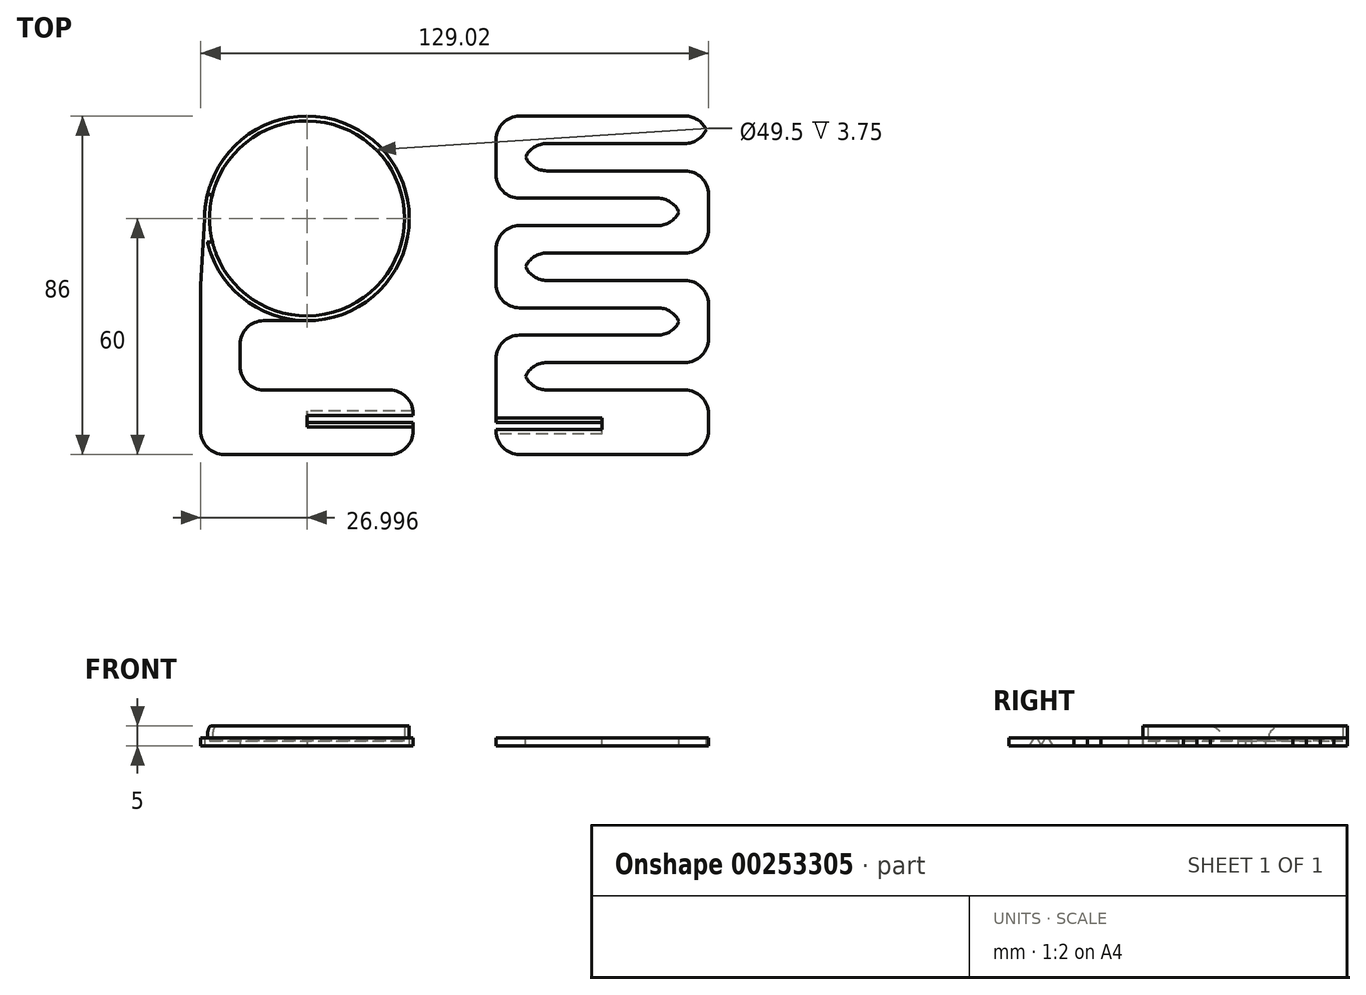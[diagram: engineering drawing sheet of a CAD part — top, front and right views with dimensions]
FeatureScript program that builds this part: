
annotation { "Feature Type Name" : "Feature", "Feature Type Description" : "" }
export const myFeature = defineFeature(function(context is Context, id is Id, definition is map)
    precondition{}
    {
        {
            var Q0;
            Q0=qCreatedBy(makeId("Top.planeOp"),FACE);
            cPlane(context, id + "F0", {"entities" : qUnion([Q0]), "cplaneType" : CPlaneType.OFFSET, "offset" : 2 * mm, "width" : 150 * mm, "height" : 150 * mm});
        }
        {
            var Q0;
            Q0=qCreatedBy(makeId("Top.planeOp"),FACE);
            var sketch = newSketch(context, id + "F1", { "sketchPlane" : qUnion([Q0])});
            skLineSegment(sketch, "E0.bottom", {"start": v(-64.51, -37.29) * mm, "end": v(-10.51, -37.29) * mm});
            skLineSegment(sketch, "E0.top", {"start": v(-64.51, 48.71) * mm, "end": v(-10.51, 48.71) * mm, "construction": true});
            skLineSegment(sketch, "E0.left", {"start": v(-64.51, -37.29) * mm, "end": v(-64.51, 48.71) * mm, "construction": true});
            skLineSegment(sketch, "E1", {"start": v(0, 56.35) * mm, "end": v(0, -54.54) * mm, "construction": true});
            skLineSegment(sketch, "E2.MirrorCS", {"start": v(64.51, 48.71) * mm, "end": v(10.51, 48.71) * mm});
            skLineSegment(sketch, "E3.MirrorCS", {"start": v(64.51, -37.29) * mm, "end": v(10.51, -37.29) * mm});
            skLineSegment(sketch, "E4.bottom", {"start": v(64.51, 41.75) * mm, "end": v(17.47, 41.75) * mm});
            skLineSegment(sketch, "E4.top", {"start": v(64.51, 34.8) * mm, "end": v(17.47, 34.8) * mm});
            skLineSegment(sketch, "E4.right", {"start": v(17.47, 41.75) * mm, "end": v(17.47, 34.8) * mm});
            skLineSegment(sketch, "E5.bottom", {"start": v(10.51, 27.83) * mm, "end": v(57.56, 27.83) * mm});
            skLineSegment(sketch, "E5.top", {"start": v(10.51, 20.88) * mm, "end": v(57.56, 20.88) * mm});
            skLineSegment(sketch, "E5.right", {"start": v(57.56, 27.83) * mm, "end": v(57.56, 20.88) * mm});
            skLineSegment(sketch, "E6.bottom", {"start": v(64.51, 13.92) * mm, "end": v(17.47, 13.92) * mm});
            skLineSegment(sketch, "E6.top", {"start": v(64.51, 6.96) * mm, "end": v(17.47, 6.96) * mm});
            skLineSegment(sketch, "E6.right", {"start": v(17.47, 13.92) * mm, "end": v(17.47, 6.96) * mm});
            skLineSegment(sketch, "E7.bottom", {"start": v(10.51, 0) * mm, "end": v(57.56, 0) * mm});
            skLineSegment(sketch, "E7.top", {"start": v(10.51, -6.96) * mm, "end": v(57.56, -6.96) * mm});
            skLineSegment(sketch, "E7.right", {"start": v(57.56, 0) * mm, "end": v(57.56, -6.96) * mm});
            skLineSegment(sketch, "E8.bottom", {"start": v(64.51, -13.92) * mm, "end": v(17.47, -13.92) * mm});
            skLineSegment(sketch, "E8.top", {"start": v(64.51, -20.88) * mm, "end": v(17.47, -20.88) * mm});
            skLineSegment(sketch, "E8.right", {"start": v(17.47, -13.92) * mm, "end": v(17.47, -20.88) * mm});
            skLineSegment(sketch, "E9", {"start": v(64.51, 48.71) * mm, "end": v(64.51, 41.75) * mm});
            skLineSegment(sketch, "E10", {"start": v(64.51, 34.8) * mm, "end": v(64.51, 13.92) * mm});
            skLineSegment(sketch, "E11", {"start": v(64.51, 6.96) * mm, "end": v(64.51, -13.92) * mm});
            skLineSegment(sketch, "E12", {"start": v(64.51, -20.88) * mm, "end": v(64.51, -37.29) * mm});
            skLineSegment(sketch, "E13", {"start": v(10.51, 48.71) * mm, "end": v(10.51, 27.83) * mm});
            skLineSegment(sketch, "E14", {"start": v(10.51, 20.88) * mm, "end": v(10.51, 0) * mm});
            skLineSegment(sketch, "E15", {"start": v(57.56, 27.83) * mm, "end": v(57.56, 34.8) * mm, "construction": true});
            skLineSegment(sketch, "E16", {"start": v(17.47, 13.92) * mm, "end": v(17.47, 20.88) * mm, "construction": true});
            skLineSegment(sketch, "E17", {"start": v(57.56, 0) * mm, "end": v(57.56, 6.96) * mm, "construction": true});
            skLineSegment(sketch, "E18", {"start": v(17.47, -13.92) * mm, "end": v(17.47, -6.96) * mm, "construction": true});
            skLineSegment(sketch, "E19", {"start": v(17.47, 34.8) * mm, "end": v(10.51, 34.8) * mm, "construction": true});
            skLineSegment(sketch, "E20", {"start": v(57.56, 20.88) * mm, "end": v(64.51, 20.88) * mm, "construction": true});
            skPoint(sketch, "E20.endSnap0", {"position": v(64.51, 24.36) * mm});
            skPoint(sketch, "E21.2.internal.snap0", {"position": v(-64.51, 5.71) * mm});
            skLineSegment(sketch, "E22", {"start": v(-64.51, 5.71) * mm, "end": v(-64.51, -37.29) * mm});
            skLineSegment(sketch, "E23.top", {"start": v(-10.51, -20.88) * mm, "end": v(-54.51, -20.88) * mm});
            skLineSegment(sketch, "E23.right", {"start": v(-54.51, -3.29) * mm, "end": v(-54.51, -20.88) * mm});
            skLineSegment(sketch, "E24", {"start": v(-54.51, -3.29) * mm, "end": v(-64.51, -3.29) * mm, "construction": true});
            skLineSegment(sketch, "E25", {"start": v(-37.51, 48.71) * mm, "end": v(-37.51, -3.29) * mm, "construction": true});
            skPoint(sketch, "E26.second.point", {"position": v(-37.51, -3.29) * mm});
            skPoint(sketch, "E26.third.point", {"position": v(-63.51, 22.71) * mm});
            skPoint(sketch, "E27.MirrorP", {"position": v(-11.51, 22.71) * mm});
            skLineSegment(sketch, "E28", {"start": v(-64.51, 5.71) * mm, "end": v(-63.51, 22.71) * mm});
            skLineSegment(sketch, "E29", {"start": v(17.47, 41.75) * mm, "end": v(17.47, 48.71) * mm, "construction": true});
            skLineSegment(sketch, "E30", {"start": v(-54.51, -3.29) * mm, "end": v(-37.51, -3.29) * mm});
            skArc(sketch, "E31", {"start": v(-63.51, 22.71) * mm, "mid": v(-55.9, 4.33) * mm, "end": v(-37.51, -3.29) * mm});
            skArc(sketch, "E32", {"start": v(-37.51, -3.29) * mm, "mid": v(-19.13, 41.1) * mm, "end": v(-63.51, 22.71) * mm, "construction": true});
            skLineSegment(sketch, "E33", {"start": v(-10.51, -20.88) * mm, "end": v(-10.51, -37.29) * mm});
            skLineSegment(sketch, "E34", {"start": v(10.51, -6.96) * mm, "end": v(10.51, -37.29) * mm});
            skLineSegment(sketch, "E35", {"start": v(-10.51, -29.08) * mm, "end": v(-64.51, -29.08) * mm, "construction": true});
            skLineSegment(sketch, "E36", {"start": v(64.51, -29.08) * mm, "end": v(10.51, -29.08) * mm, "construction": true});
            skSolve(sketch);
        }
        {
            var Q0;
            Q0=qCreatedBy(makeId("Top.planeOp"),FACE);
            var sketch = newSketch(context, id + "F2", { "sketchPlane" : qUnion([Q0])});
            skCircle(sketch, "E37", {"center": v(-37.51, 22.71) * mm, "radius": 26 * mm});
            skPoint(sketch, "E37.first.point", {"position": v(-37.51, 48.71) * mm});
            skPoint(sketch, "E37.second.point", {"position": v(-37.51, -3.29) * mm});
            skPoint(sketch, "E37.third.point", {"position": v(-63.51, 22.71) * mm});
            skSolve(sketch);
        }
        {
            var Q0;
            Q0=qCreatedBy(id+"F0.planeOp",FACE);
            var sketch = newSketch(context, id + "F3", { "sketchPlane" : qUnion([Q0])});
            skLineSegment(sketch, "E38.bottom", {"start": v(-67.51, 28.71) * mm, "end": v(-59.51, 28.71) * mm});
            skLineSegment(sketch, "E38.top", {"start": v(-67.51, 16.71) * mm, "end": v(-59.51, 16.71) * mm});
            skLineSegment(sketch, "E38.left", {"start": v(-67.51, 28.71) * mm, "end": v(-67.51, 16.71) * mm});
            skLineSegment(sketch, "E38.right", {"start": v(-59.51, 28.71) * mm, "end": v(-59.51, 16.71) * mm});
            skPoint(sketch, "E38.middle", {"position": v(-63.51, 22.71) * mm});
            skSolve(sketch);
        }
        {
            var Q0;
            Q0=qCreatedBy(makeId("Top.planeOp"),FACE);
            var sketch = newSketch(context, id + "F4", { "sketchPlane" : qUnion([Q0])});
            skLineSegment(sketch, "E39.bottom", {"start": v(-10.51, -33.93) * mm, "end": v(-37.51, -33.93) * mm});
            skLineSegment(sketch, "E39.top", {"start": v(-10.51, -24.24) * mm, "end": v(-37.51, -24.24) * mm});
            skLineSegment(sketch, "E39.left", {"start": v(-10.51, -33.93) * mm, "end": v(-10.51, -24.24) * mm});
            skLineSegment(sketch, "E39.right", {"start": v(-37.51, -33.93) * mm, "end": v(-37.51, -24.24) * mm});
            skPoint(sketch, "E39.middle", {"position": v(-24.01, -29.08) * mm});
            skSolve(sketch);
        }
        {
            var Q0;
            Q0=qCreatedBy(makeId("Top.planeOp"),FACE);
            var sketch = newSketch(context, id + "F5", { "sketchPlane" : qUnion([Q0])});
            skLineSegment(sketch, "E40.bottom", {"start": v(37.51, -24.24) * mm, "end": v(10.51, -24.24) * mm});
            skLineSegment(sketch, "E40.top", {"start": v(37.51, -33.93) * mm, "end": v(10.51, -33.93) * mm});
            skLineSegment(sketch, "E40.left", {"start": v(37.51, -24.24) * mm, "end": v(37.51, -33.93) * mm});
            skLineSegment(sketch, "E40.right", {"start": v(10.51, -24.24) * mm, "end": v(10.51, -33.93) * mm});
            skPoint(sketch, "E40.middle", {"position": v(24.01, -29.08) * mm});
            skSolve(sketch);
        }
        {
            var Q0;
            Q0 = qSketchRegion(id + "F1", true);
            extrude(context, id + "F6", {"entities" : qUnion([Q0]), "depth" : 2 * mm});
        }
        {
            var Q0;
            Q0=makeQuery(id+"F6.opExtrude","SWEPT_EDGE",EDGE,{"disambiguationData":[OSD([sQuery(id+"F1.wireOp",EDGE,"E4.bottom"),sQuery(id+"F1.wireOp",EDGE,"E4.right")])]});
            var Q1;
            Q1=makeQuery(id+"F6.opExtrude","SWEPT_EDGE",EDGE,{"disambiguationData":[OSD([sQuery(id+"F1.wireOp",EDGE,"E6.bottom"),sQuery(id+"F1.wireOp",EDGE,"E6.right")])]});
            var Q2;
            Q2=makeQuery(id+"F6.opExtrude","SWEPT_EDGE",EDGE,{"disambiguationData":[OSD([sQuery(id+"F1.wireOp",EDGE,"E8.bottom"),sQuery(id+"F1.wireOp",EDGE,"E8.right")])]});
            var Q3;
            Q3=makeQuery(id+"F6.opExtrude","SWEPT_EDGE",EDGE,{"disambiguationData":[OSD([sQuery(id+"F1.wireOp",EDGE,"E8.top"),sQuery(id+"F1.wireOp",EDGE,"E12")])]});
            var Q4;
            Q4=makeQuery(id+"F6.opExtrude","SWEPT_EDGE",EDGE,{"disambiguationData":[OSD([sQuery(id+"F1.wireOp",EDGE,"E8.bottom"),sQuery(id+"F1.wireOp",EDGE,"E11")])]});
            var Q5;
            Q5=makeQuery(id+"F6.opExtrude","SWEPT_EDGE",EDGE,{"disambiguationData":[OSD([sQuery(id+"F1.wireOp",EDGE,"E6.top"),sQuery(id+"F1.wireOp",EDGE,"E11")])]});
            var Q6;
            Q6=makeQuery(id+"F6.opExtrude","SWEPT_EDGE",EDGE,{"disambiguationData":[OSD([sQuery(id+"F1.wireOp",EDGE,"E6.bottom"),sQuery(id+"F1.wireOp",EDGE,"E10")])]});
            var Q7;
            Q7=makeQuery(id+"F6.opExtrude","SWEPT_EDGE",EDGE,{"disambiguationData":[OSD([sQuery(id+"F1.wireOp",EDGE,"E4.top"),sQuery(id+"F1.wireOp",EDGE,"E10")])]});
            var Q8;
            Q8=makeQuery(id+"F6.opExtrude","SWEPT_EDGE",EDGE,{"disambiguationData":[OSD([sQuery(id+"F1.wireOp",EDGE,"E2.MirrorCS"),sQuery(id+"F1.wireOp",EDGE,"E9")])]});
            var Q9;
            Q9=makeQuery(id+"F6.opExtrude","SWEPT_EDGE",EDGE,{"disambiguationData":[OSD([sQuery(id+"F1.wireOp",EDGE,"E3.MirrorCS"),sQuery(id+"F1.wireOp",EDGE,"E12")])]});
            var Q10;
            Q10=makeQuery(id+"F6.opExtrude","SWEPT_EDGE",EDGE,{"disambiguationData":[OSD([sQuery(id+"F1.wireOp",EDGE,"E3.MirrorCS"),sQuery(id+"F1.wireOp",EDGE,"b5c075ea-845a-4698-b512-59f1e6f9d4d20.MirrorCS")])]});
            var Q11;
            Q11=makeQuery(id+"F6.opExtrude","SWEPT_EDGE",EDGE,{"disambiguationData":[OSD([sQuery(id+"F1.wireOp",EDGE,"E0.bottom"),sQuery(id+"F1.wireOp",EDGE,"YFyWnAeK-pBBA-IvNz-k6wc-S340Zklw97iA")])]});
            var Q12;
            Q12=makeQuery(id+"F6.opExtrude","SWEPT_EDGE",EDGE,{"disambiguationData":[OSD([sQuery(id+"F1.wireOp",EDGE,"E0.bottom"),sQuery(id+"F1.wireOp",EDGE,"E0.left")])]});
            var Q13;
            Q13=makeQuery(id+"F6.opExtrude","SWEPT_EDGE",EDGE,{"disambiguationData":[OSD([sQuery(id+"F1.wireOp",EDGE,"E0.top"),sQuery(id+"F1.wireOp",EDGE,"n8BnLhJH-u2Um-0aWn-nEOY-44NhoaiNVUQD")])]});
            var Q14;
            Q14=makeQuery(id+"F6.opExtrude","SWEPT_EDGE",EDGE,{"disambiguationData":[OSD([sQuery(id+"F1.wireOp",EDGE,"E4.top"),sQuery(id+"F1.wireOp",EDGE,"E4.right")])]});
            var Q15;
            Q15=makeQuery(id+"F6.opExtrude","SWEPT_EDGE",EDGE,{"disambiguationData":[OSD([sQuery(id+"F1.wireOp",EDGE,"E6.top"),sQuery(id+"F1.wireOp",EDGE,"E6.right")])]});
            var Q16;
            Q16=makeQuery(id+"F6.opExtrude","SWEPT_EDGE",EDGE,{"disambiguationData":[OSD([sQuery(id+"F1.wireOp",EDGE,"E5.top"),sQuery(id+"F1.wireOp",EDGE,"E14")])]});
            var Q17;
            Q17=makeQuery(id+"F6.opExtrude","SWEPT_EDGE",EDGE,{"disambiguationData":[OSD([sQuery(id+"F1.wireOp",EDGE,"E7.top"),sQuery(id+"F1.wireOp",EDGE,"ZmS6kUhB-3YoN-C8Cs-CpPg-u5vmyANZ6dh0")])]});
            var Q18;
            Q18=makeQuery(id+"F6.opExtrude","SWEPT_EDGE",EDGE,{"disambiguationData":[OSD([sQuery(id+"F1.wireOp",EDGE,"E2.MirrorCS"),sQuery(id+"F1.wireOp",EDGE,"E13")])]});
            var Q19;
            Q19=makeQuery(id+"F6.opExtrude","SWEPT_EDGE",EDGE,{"disambiguationData":[OSD([sQuery(id+"F1.wireOp",EDGE,"E8.top"),sQuery(id+"F1.wireOp",EDGE,"E8.right")])]});
            var Q20;
            Q20=makeQuery(id+"F6.opExtrude","SWEPT_EDGE",EDGE,{"disambiguationData":[OSD([sQuery(id+"F1.wireOp",EDGE,"E7.bottom"),sQuery(id+"F1.wireOp",EDGE,"E7.right")])]});
            var Q21;
            Q21=makeQuery(id+"F6.opExtrude","SWEPT_EDGE",EDGE,{"disambiguationData":[OSD([sQuery(id+"F1.wireOp",EDGE,"E7.bottom"),sQuery(id+"F1.wireOp",EDGE,"E14")])]});
            var Q22;
            Q22=makeQuery(id+"F6.opExtrude","SWEPT_EDGE",EDGE,{"disambiguationData":[OSD([sQuery(id+"F1.wireOp",EDGE,"02cee5f8-0e07-4a12-8da6-797b128053240.MirrorCS"),sQuery(id+"F1.wireOp",EDGE,"ZmS6kUhB-3YoN-C8Cs-CpPg-u5vmyANZ6dh0")])]});
            var Q23;
            Q23=makeQuery(id+"F6.opExtrude","SWEPT_EDGE",EDGE,{"disambiguationData":[OSD([sQuery(id+"F1.wireOp",EDGE,"E5.bottom"),sQuery(id+"F1.wireOp",EDGE,"E13")])]});
            var Q24;
            Q24=makeQuery(id+"F6.opExtrude","SWEPT_EDGE",EDGE,{"disambiguationData":[OSD([sQuery(id+"F1.wireOp",EDGE,"E5.bottom"),sQuery(id+"F1.wireOp",EDGE,"E5.right")])]});
            var Q25;
            Q25=makeQuery(id+"F6.opExtrude","SWEPT_EDGE",EDGE,{"disambiguationData":[OSD([sQuery(id+"F1.wireOp",EDGE,"E0.top"),sQuery(id+"F1.wireOp",EDGE,"E0.left")])]});
            var Q26;
            Q26=makeQuery(id+"F6.opExtrude","SWEPT_EDGE",EDGE,{"disambiguationData":[OSD([sQuery(id+"F1.wireOp",EDGE,"E5.top"),sQuery(id+"F1.wireOp",EDGE,"E5.right")])]});
            var Q27;
            Q27=makeQuery(id+"F6.opExtrude","SWEPT_EDGE",EDGE,{"disambiguationData":[OSD([sQuery(id+"F1.wireOp",EDGE,"E7.top"),sQuery(id+"F1.wireOp",EDGE,"E7.right")])]});
            var Q28;
            Q28=makeQuery(id+"F6.opExtrude","SWEPT_EDGE",EDGE,{"disambiguationData":[OSD([sQuery(id+"F1.wireOp",EDGE,"E23.top"),sQuery(id+"F1.wireOp",EDGE,"E23.right")])]});
            var Q29;
            Q29=makeQuery(id+"F6.opExtrude","SWEPT_EDGE",EDGE,{"disambiguationData":[OSD([sQuery(id+"F1.wireOp",EDGE,"E23.top"),sQuery(id+"F1.wireOp",EDGE,"a9DOpzYk-i0cr-7vyi-HXUP-g6eablmnLJva")])]});
            var Q30;
            Q30=makeQuery(id+"F6.opExtrude","SWEPT_EDGE",EDGE,{"disambiguationData":[OSD([sQuery(id+"F1.wireOp",EDGE,"E23.bottom"),sQuery(id+"F1.wireOp",EDGE,"lBwJjgHI-4274-be9I-VBba-0aZR1f0Lvly4")])]});
            var Q31;
            Q31=makeQuery(id+"F6.opExtrude","SWEPT_EDGE",EDGE,{"disambiguationData":[OSD([sQuery(id+"F1.wireOp",EDGE,"E23.bottom"),sQuery(id+"F1.wireOp",EDGE,"E23.right")])]});
            var Q32;
            Q32=makeQuery(id+"F6.opExtrude","SWEPT_EDGE",EDGE,{"disambiguationData":[OSD([sQuery(id+"F1.wireOp",EDGE,"E4.bottom"),sQuery(id+"F1.wireOp",EDGE,"E9")])]});
            fillet(context, id + "F7", {"entities" : qUnion([Q0, Q1, Q2, Q3, Q4, Q5, Q6, Q7, Q8, Q9, Q10, Q11, Q12, Q13, Q14, Q15, Q16, Q17, Q18, Q19, Q20, Q21, Q22, Q23, Q24, Q25, Q26, Q27, Q28, Q29, Q30, Q31, Q32]), "radius" : 6 * mm, "tangentPropagation" : true, "allowEdgeOverflow" : false});
        }
        {
            var Q0;
            Q0 = qSketchRegion(id + "F2", true);
            extrude(context, id + "F8", {"entities" : qUnion([Q0]), "operationType" : NewBodyOperationType.ADD, "depth" : 5 * mm});
        }
        {
            var Q0;
            Q0=makeQuery(id+"F8.opExtrude","CAP_FACE",FACE,{"disambiguationData":[OSD([sQuery(id+"F2.wireOp",EDGE,"E37")])],"isStart":false});
            shell(context, id + "F9", {"entities" : qUnion([Q0]), "thickness" : 1.25 * mm});
        }
        {
            var Q0;
            Q0 = qSketchRegion(id + "F3", true);
            extrude(context, id + "F10", {"entities" : qUnion([Q0]), "operationType" : NewBodyOperationType.REMOVE, "depth" : 5 * mm});
        }
        {
            var Q0;
            Q0=makeQuery(id+"F10.boolean.opBoolean","INTERSECT",EDGE,{"derivedFrom":[makeQuery(id+"F8.opExtrude","CAP_FACE",FACE,{"disambiguationData":[OSD([sQuery(id+"F2.wireOp",EDGE,"E37")])],"isStart":false}),makeQuery(id+"F10.opExtrude","SWEPT_FACE",FACE,{"disambiguationData":[OSD([sQuery(id+"F3.wireOp",EDGE,"E38.bottom")])]})]});
            var Q1;
            Q1=makeQuery(id+"F10.boolean.opBoolean","INTERSECT",EDGE,{"derivedFrom":[makeQuery(id+"F8.opExtrude","CAP_FACE",FACE,{"disambiguationData":[OSD([sQuery(id+"F2.wireOp",EDGE,"E37")])],"isStart":false}),makeQuery(id+"F10.opExtrude","SWEPT_FACE",FACE,{"disambiguationData":[OSD([sQuery(id+"F3.wireOp",EDGE,"E38.top")])]})]});
            fillet(context, id + "F11", {"entities" : qUnion([Q0, Q1]), "radius" : 3 * mm, "tangentPropagation" : true, "allowEdgeOverflow" : false});
        }
        {
            var Q0;
            Q0 = qSketchRegion(id + "F4", true);
            extrude(context, id + "F12", {"entities" : qUnion([Q0]), "depth" : 2.5 * mm});
        }
        {
            var Q0;
            Q0 = qSketchRegion(id + "F5", true);
            extrude(context, id + "F13", {"entities" : qUnion([Q0]), "depth" : 2.5 * mm});
        }
        {
            var Q0;
            Q0=makeQuery(id+"F12.opExtrude","SWEPT_BODY",BODY,{"disambiguationData":[OSD([sQuery(id+"F4.wireOp",EDGE,"E39.bottom"),sQuery(id+"F4.wireOp",EDGE,"E39.top"),sQuery(id+"F4.wireOp",EDGE,"E39.left"),sQuery(id+"F4.wireOp",EDGE,"E39.right")])]});
            var Q1;
            Q1=sQuery(id+"F1.wireOp",EDGE,"E35");
            transform(context, id + "F14", {"entities" : qUnion([Q0]), "transformType" : TransformType.ROTATION, "transformAxis" : qUnion([Q1]), "angle" : 60 * degree, "makeCopy" : false});
        }
        {
            var Q0;
            Q0=makeQuery(id+"F13.opExtrude","SWEPT_BODY",BODY,{"disambiguationData":[OSD([sQuery(id+"F5.wireOp",EDGE,"E40.bottom"),sQuery(id+"F5.wireOp",EDGE,"E40.top"),sQuery(id+"F5.wireOp",EDGE,"E40.left"),sQuery(id+"F5.wireOp",EDGE,"E40.right")])]});
            var Q1;
            Q1=sQuery(id+"F1.wireOp",EDGE,"E36");
            transform(context, id + "F15", {"entities" : qUnion([Q0]), "transformType" : TransformType.ROTATION, "transformAxis" : qUnion([Q1]), "angle" : 120 * degree, "makeCopy" : false});
        }
        {
            var Q0;
            Q0=makeQuery(id+"F13.opExtrude","SWEPT_BODY",BODY,{"disambiguationData":[OSD([sQuery(id+"F5.wireOp",EDGE,"E40.bottom"),sQuery(id+"F5.wireOp",EDGE,"E40.top"),sQuery(id+"F5.wireOp",EDGE,"E40.left"),sQuery(id+"F5.wireOp",EDGE,"E40.right")])]});
            transform(context, id + "F16", {"entities" : qUnion([Q0]), "transformType" : TransformType.TRANSLATION_3D, "dx" : 0 * mm, "dy" : -3 * mm, "dz" : 0 * mm, "makeCopy" : false});
        }
        {
            var Q0;
            Q0=makeQuery(id+"F12.opExtrude","SWEPT_BODY",BODY,{"disambiguationData":[OSD([sQuery(id+"F4.wireOp",EDGE,"E39.bottom"),sQuery(id+"F4.wireOp",EDGE,"E39.top"),sQuery(id+"F4.wireOp",EDGE,"E39.left"),sQuery(id+"F4.wireOp",EDGE,"E39.right")])]});
            var Q1;
            Q1=makeQuery(id+"F13.opExtrude","SWEPT_BODY",BODY,{"disambiguationData":[OSD([sQuery(id+"F5.wireOp",EDGE,"E40.bottom"),sQuery(id+"F5.wireOp",EDGE,"E40.top"),sQuery(id+"F5.wireOp",EDGE,"E40.left"),sQuery(id+"F5.wireOp",EDGE,"E40.right")])]});
            var Q2;
            Q2=makeQuery(id+"F6.opExtrude","SWEPT_BODY",BODY,{"disambiguationData":[OSD([sQuery(id+"F1.wireOp",EDGE,"E0.bottom"),sQuery(id+"F1.wireOp",EDGE,"E22"),sQuery(id+"F1.wireOp",EDGE,"E23.top"),sQuery(id+"F1.wireOp",EDGE,"E23.right"),sQuery(id+"F1.wireOp",EDGE,"E28"),sQuery(id+"F1.wireOp",EDGE,"E30"),sQuery(id+"F1.wireOp",EDGE,"E31"),sQuery(id+"F1.wireOp",EDGE,"E33")])]});
            var Q3;
            Q3=makeQuery(id+"F6.opExtrude","SWEPT_BODY",BODY,{"disambiguationData":[OSD([sQuery(id+"F1.wireOp",EDGE,"E2.MirrorCS"),sQuery(id+"F1.wireOp",EDGE,"E3.MirrorCS"),sQuery(id+"F1.wireOp",EDGE,"E4.bottom"),sQuery(id+"F1.wireOp",EDGE,"E4.top"),sQuery(id+"F1.wireOp",EDGE,"E4.right"),sQuery(id+"F1.wireOp",EDGE,"E5.bottom"),sQuery(id+"F1.wireOp",EDGE,"E5.top"),sQuery(id+"F1.wireOp",EDGE,"E5.right"),sQuery(id+"F1.wireOp",EDGE,"E6.bottom"),sQuery(id+"F1.wireOp",EDGE,"E6.top"),sQuery(id+"F1.wireOp",EDGE,"E6.right"),sQuery(id+"F1.wireOp",EDGE,"E7.bottom"),sQuery(id+"F1.wireOp",EDGE,"E7.top"),sQuery(id+"F1.wireOp",EDGE,"E7.right"),sQuery(id+"F1.wireOp",EDGE,"E8.bottom"),sQuery(id+"F1.wireOp",EDGE,"E8.top"),sQuery(id+"F1.wireOp",EDGE,"E8.right"),sQuery(id+"F1.wireOp",EDGE,"E9"),sQuery(id+"F1.wireOp",EDGE,"E10"),sQuery(id+"F1.wireOp",EDGE,"E11"),sQuery(id+"F1.wireOp",EDGE,"E12"),sQuery(id+"F1.wireOp",EDGE,"E13"),sQuery(id+"F1.wireOp",EDGE,"E14"),sQuery(id+"F1.wireOp",EDGE,"E34")])]});
            booleanBodies(context, id + "F17", {"operationType" : BooleanOperationType.SUBTRACTION, "tools" : qUnion([Q0, Q1]), "targets" : qUnion([Q2, Q3])});
        }
    });
